# Revit family: 1GAHP-A
name_source: partatom
category: Wyposażenie mechaniczne
revit_build: Autodesk Revit 2015 (Build: 20160512_1515(x64)
units: mm (PartAtom-declared; Revit-internal decimal feet)

## types (2) — shared parameters
Autor = www.archispace.pl
Ciśnienie gazu zasilającego (LPG G30/G31) = 32 - 42 mbar
Ciśnienie gazu zasilającego (gaz ziemny G20) = 17 - 23 mbar
Dokumentacja techniczna = http://www.gazuno.pl
Dopuszczalny spadek ciśnienia na wentylatorze = 40.0 Pa
Głębokość = 1260 mm  [stored 4.13386 ft]
IP = X5D
Ilość wody w urządzeniu = 4.0 L
Klasyfikacja obciążenia = Inne
Maksymalne ciśnienie robocze = 4 pasek
Materiał obudowa 1 = Robur_CashmereGrey
Materiał obudowa 2 = Robur_Czarny
Materiał podstawa = Robur_Stal
Max. ciśnienie w układzie absorpcyjnym = 32 bar
Max. przepływ kondensatu = 4 l/h
Max. przepływ wody grzewczej = 1.111 L/s
Max. temperatura powietrza zewnętrznego = 40 °C
Max. temperatura wody na wejściu do urządzenia (dla ogrzewania) = 55 °C
Max. temperatura wody na wyjściu z urządzenia = 65 °C
Min. przepływ wody grzewczej = 0.389 L/s
Min. temperatura powietrza zewnętrznego = -30 °C
Min. temperatura wody na wejściu do urządzenia (podczas pracy ciągłej) = 20 °C
Napięcie zasilania = 230 V
Nominalna moc grzewcza palnika = 25700 W
Nominalny przepływ wody grzewczej = 0.833 L/s
Nominalny spadek ciśnienia wody grzewczej = 0.43 pasek
Opis = Powietrzna absorpcyjna pompa ciepła zasilana gazem i energią odnawialną.
Producent = Robur
Przepływ powietrza przez wymiennik lamelowy (parownik) = 11000 m³/h
Rzeczywista moc grzewcza palnika = 25200 W
Sposób instalacji = B23P, B33, B53P
Szerokość = 854 mm  [stored 2.80184 ft]
URL = www.gazuno.pl
Waga płynu roboczego - amoniak R717 = 7.00 kg
Waga płynu roboczego - woda = 10.00 kg
Współczynnik mocy = 1

## per-type parameters (varying)
| type | Ciśnienie akustyczne w odległości 5 metrów | Moc elektryczna | Obciążenie pozorne | S1 | STD | Waga | Wysokość |
| GAHP-A HT | 57,6 dB (A) | 840 W | 840 VA | Nie | Tak | 390.00 kg | 1445 mm |
| GAHP-A HT S1 | 52 dB (A) | 770 W | 770 VA | Tak | Nie | 400.00 kg | 1536 mm  [stored 5.03937 ft] |

note: column(s) folded — value = type name in every type: Model

note: [stored X ft] marks values corroborated as IEEE doubles in the binary element streams (Revit-internal decimal feet)
